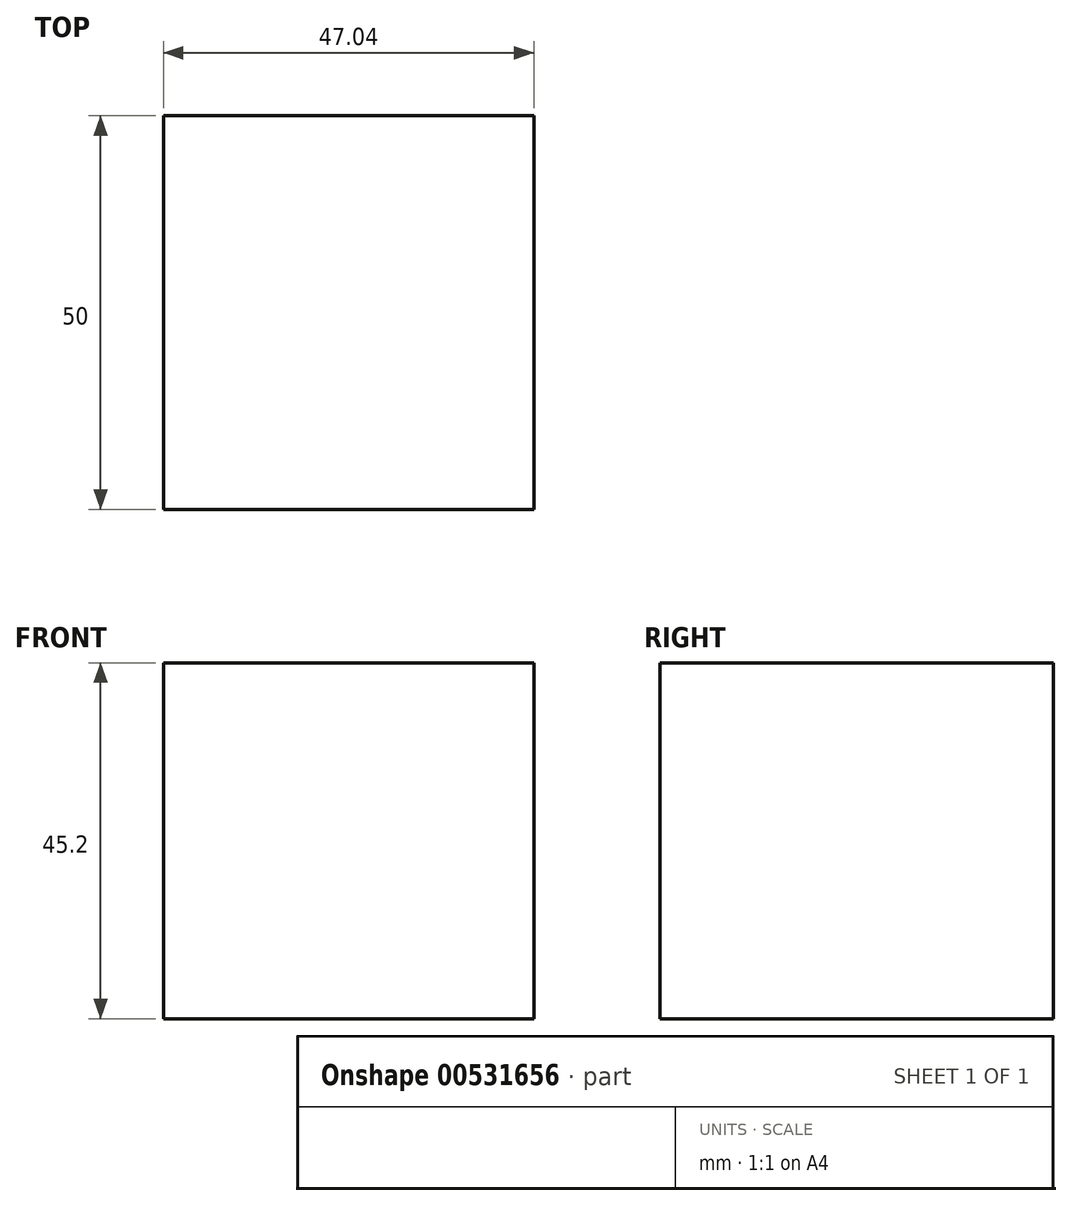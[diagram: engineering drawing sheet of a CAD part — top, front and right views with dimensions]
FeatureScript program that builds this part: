
annotation { "Feature Type Name" : "Feature", "Feature Type Description" : "" }
export const myFeature = defineFeature(function(context is Context, id is Id, definition is map)
    precondition{}
    {
        {
            var Q0;
            Q0=qCreatedBy(makeId("Front.planeOp"),FACE);
            var sketch = newSketch(context, id + "F0", { "sketchPlane" : qUnion([Q0])});
            skLineSegment(sketch, "E0.bottom", {"start": v(31.55, -6.68) * mm, "end": v(-50.27, -6.68) * mm});
            skLineSegment(sketch, "E0.top", {"start": v(31.55, 56.68) * mm, "end": v(-50.27, 56.68) * mm});
            skLineSegment(sketch, "E0.left", {"start": v(31.55, -6.68) * mm, "end": v(31.55, 56.68) * mm});
            skLineSegment(sketch, "E0.right", {"start": v(-50.27, -6.68) * mm, "end": v(-50.27, 56.68) * mm});
            skLineSegment(sketch, "E1.bottom", {"start": v(-15.5, 38.52) * mm, "end": v(31.55, 38.52) * mm});
            skLineSegment(sketch, "E1.top", {"start": v(-15.5, -6.68) * mm, "end": v(31.55, -6.68) * mm});
            skLineSegment(sketch, "E1.left", {"start": v(-15.5, 38.52) * mm, "end": v(-15.5, -6.68) * mm});
            skLineSegment(sketch, "E1.right", {"start": v(31.55, 38.52) * mm, "end": v(31.55, -6.68) * mm});
            skSolve(sketch);
        }
        {
            var Q0;
            Q0 = qSketchRegion(id + "F0", true);
            var sketch = newSketch(context, id + "F1", { "sketchPlane" : qUnion([Q0])});
            skSolve(sketch);
        }
        {
            var Q0;
            Q0 = qSketchRegion(id + "F1", true);
            var Q1;
            Q1=makeQuery(id+"F0.imprint","IMPRINT",FACE,{"disambiguationData":[TD([[makeQuery(id+"F0.imprint","IMPRINT",EDGE,{"derivedFrom":sQuery(id+"F0.wireOp",EDGE,"E0.bottom")}),-1.0]])]});
            extrude(context, id + "F2", {"entities" : qUnion([Q0, Q1]), "depth" : 50 * mm, "offsetDistance" : 25.4 * mm});
        }
    });
